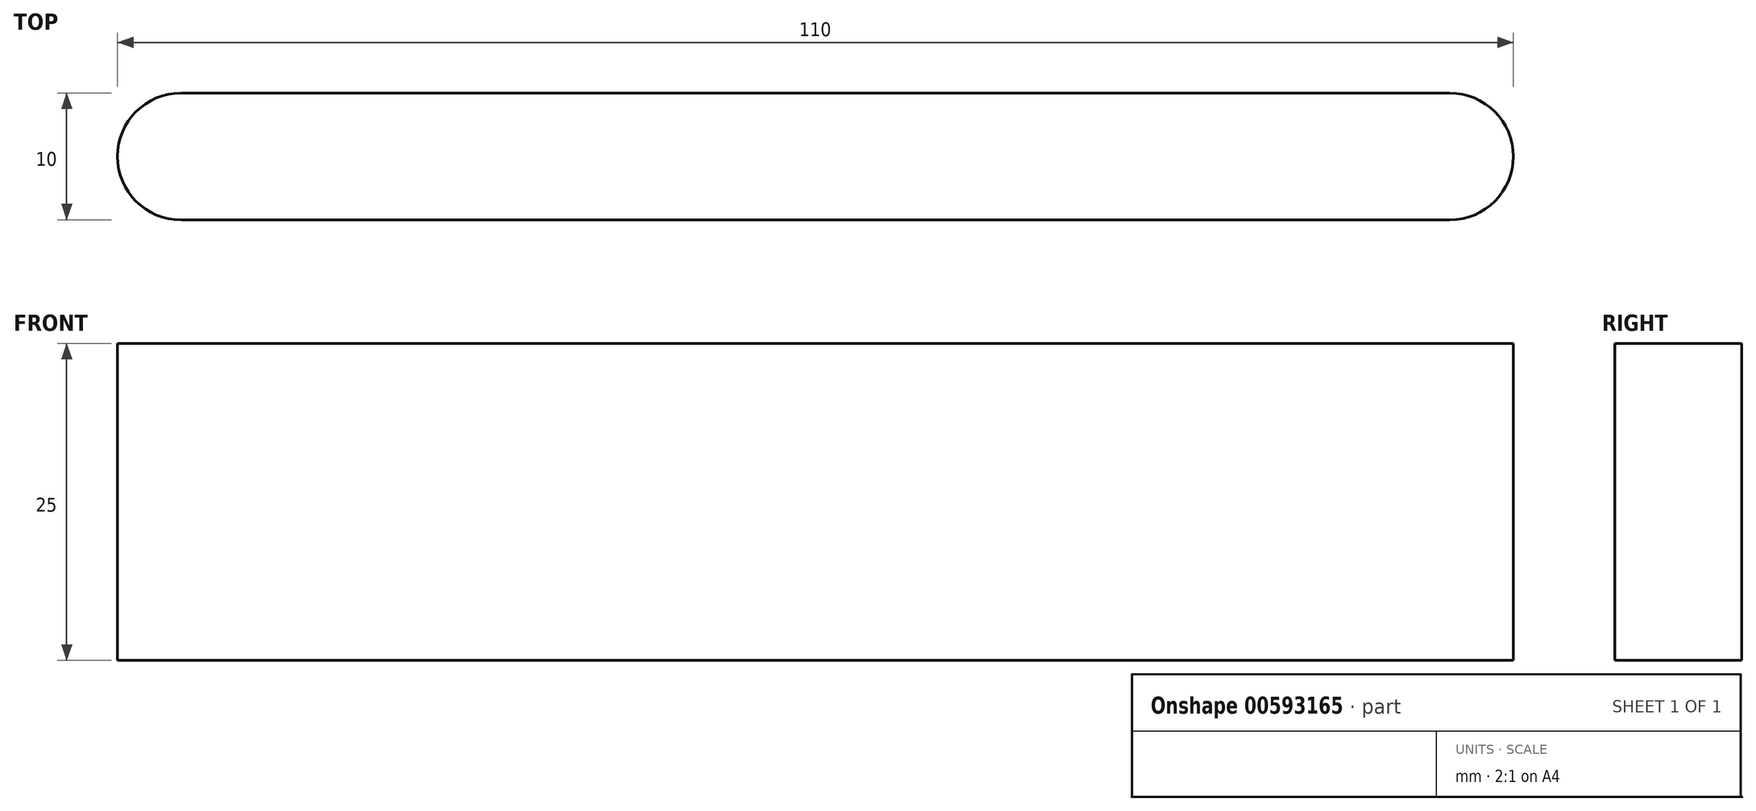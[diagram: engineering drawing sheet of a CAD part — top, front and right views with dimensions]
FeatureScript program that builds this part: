
annotation { "Feature Type Name" : "Feature", "Feature Type Description" : "" }
export const myFeature = defineFeature(function(context is Context, id is Id, definition is map)
    precondition{}
    {
        {
            var Q0;
            Q0=qCreatedBy(makeId("Top.planeOp"),FACE);
            var sketch = newSketch(context, id + "F0", { "sketchPlane" : qUnion([Q0])});
            skLineSegment(sketch, "E0.bottom", {"start": v(-17.5, 25.48) * mm, "end": v(82.5, 25.48) * mm});
            skLineSegment(sketch, "E0.top", {"start": v(-17.5, 15.48) * mm, "end": v(82.5, 15.48) * mm});
            skLineSegment(sketch, "E0.left", {"start": v(-17.5, 25.48) * mm, "end": v(-17.5, 15.48) * mm});
            skLineSegment(sketch, "E0.right", {"start": v(82.5, 25.48) * mm, "end": v(82.5, 15.48) * mm});
            skCircle(sketch, "E1", {"center": v(-17.5, 20.48) * mm, "radius": 5 * mm});
            skCircle(sketch, "E2", {"center": v(82.5, 20.48) * mm, "radius": 5 * mm});
            skSolve(sketch);
        }
        {
            var Q0;
            Q0 = qSketchRegion(id + "F0", true);
            extrude(context, id + "F1", {"entities" : qUnion([Q0]), "depth" : 25 * mm, "offsetDistance" : 25 * mm});
        }
    });
